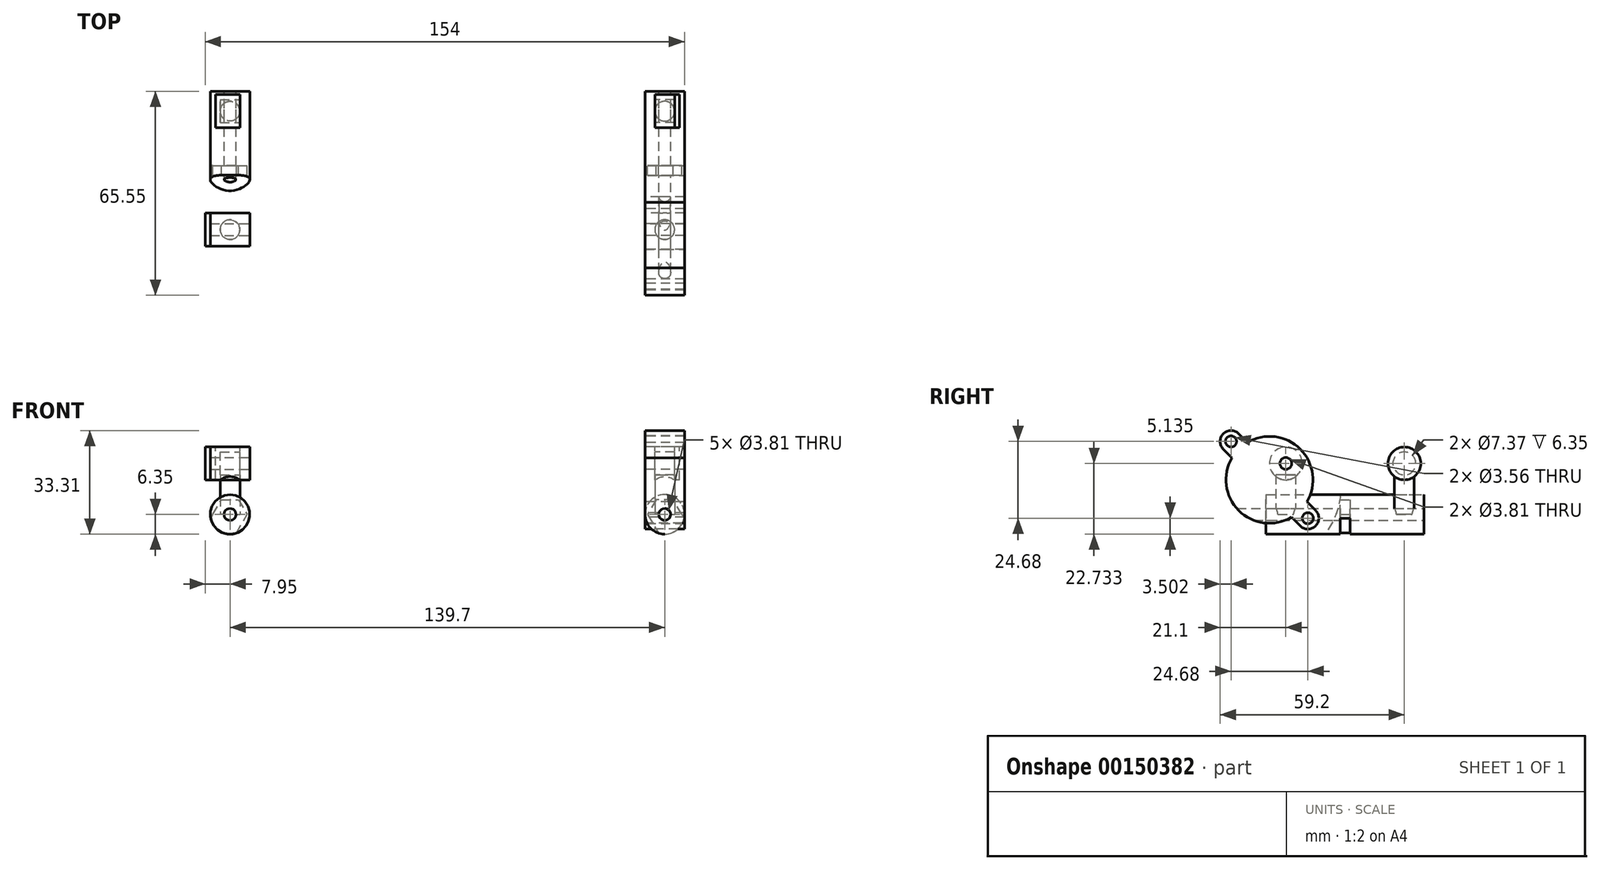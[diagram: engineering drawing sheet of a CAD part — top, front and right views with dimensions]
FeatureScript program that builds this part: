
annotation { "Feature Type Name" : "Feature", "Feature Type Description" : "" }
export const myFeature = defineFeature(function(context is Context, id is Id, definition is map)
    precondition{}
    {
        {
            var Q0;
            Q0=qCreatedBy(makeId("Front.planeOp"),FACE);
            var sketch = newSketch(context, id + "F0", { "sketchPlane" : qUnion([Q0])});
            skCircle(sketch, "E0", {"center": v(-69.85, 0) * mm, "radius": 1.9 * mm});
            skCircle(sketch, "E1", {"center": v(69.85, 0) * mm, "radius": 1.9 * mm});
            skLineSegment(sketch, "E2", {"start": v(-69.85, 0) * mm, "end": v(0, 0) * mm, "construction": true});
            skLineSegment(sketch, "E3", {"start": v(69.85, 0) * mm, "end": v(0, 0) * mm, "construction": true});
            skArc(sketch, "E4", {"start": v(-69.85, 6.35) * mm, "mid": v(-74.34, -4.5) * mm, "end": v(-63.5, 0) * mm});
            skArc(sketch, "E5", {"start": v(63.5, 0) * mm, "mid": v(74.34, -4.5) * mm, "end": v(69.85, 6.35) * mm});
            skLineSegment(sketch, "E6", {"start": v(69.85, 6.35) * mm, "end": v(69.85, 0) * mm, "construction": true});
            skLineSegment(sketch, "E7", {"start": v(-69.85, 6.35) * mm, "end": v(-69.85, 0) * mm, "construction": true});
            skArc(sketch, "E8", {"start": v(-63.5, 0) * mm, "mid": v(-65.36, 4.5) * mm, "end": v(-69.85, 6.35) * mm});
            skArc(sketch, "E9", {"start": v(69.85, 6.35) * mm, "mid": v(65.36, 4.5) * mm, "end": v(63.5, 0) * mm});
            skSolve(sketch);
        }
        {
            var Q0;
            Q0 = qSketchRegion(id + "F0", true);
            extrude(context, id + "F1", {"entities" : qUnion([Q0]), "endBound" : BoundingType.SYMMETRIC, "depth" : 12.7 * mm});
        }
        {
            var Q0;
            Q0=makeQuery(id+"F1.opExtrude","CAP_FACE",FACE,{"disambiguationData":[OSD([sQuery(id+"F0.wireOp",EDGE,"E0"),sQuery(id+"F0.wireOp",EDGE,"E1"),sQuery(id+"F0.wireOp",EDGE,"E4"),sQuery(id+"F0.wireOp",EDGE,"E5"),sQuery(id+"F0.wireOp",EDGE,"xyxUVOh0-Lu6m-2nq8-UmFe-XEndblqHEdPT"),sQuery(id+"F0.wireOp",EDGE,"R0XNFQHJ-87U4-ma3Q-qhns-AWXhGPeFOJpI"),sQuery(id+"F0.wireOp",EDGE,"e34iIN8D-vhv8-jKHx-9azW-8f77yfFPg5bW"),sQuery(id+"F0.wireOp",EDGE,"8HNf8llB-7DT9-wTKg-WSqf-SX1znclEPI6e"),sQuery(id+"F0.wireOp",EDGE,"dpBhEA3d-197v-VctA-TAhr-BlY7lmP6uD7G"),sQuery(id+"F0.wireOp",EDGE,"sEkqqTot-DNnZ-R70t-ELHf-v8sBDht2CAfZ")])],"isStart":false});
            var sketch = newSketch(context, id + "F2", { "sketchPlane" : qUnion([Q0])});
            skCircle(sketch, "E10.0", {"center": v(-69.85, 0) * mm, "radius": 1.9 * mm});
            skLineSegment(sketch, "E10.1", {"start": v(-64.48, 3.39) * mm, "end": v(-64.48, 3.39) * mm});
            skLineSegment(sketch, "E11.MirrorCS", {"start": v(64.48, 3.39) * mm, "end": v(64.48, 3.39) * mm});
            skCircle(sketch, "E12.MirrorC", {"center": v(69.85, 0) * mm, "radius": 1.9 * mm});
            skCircle(sketch, "E13.0", {"center": v(69.85, 0) * mm, "radius": 6.35 * mm});
            skCircle(sketch, "E13.1", {"center": v(-69.85, 0) * mm, "radius": 6.35 * mm});
            skSolve(sketch);
        }
        {
            var Q0;
            Q0 = qSketchRegion(id + "F2", true);
            extrude(context, id + "F3", {"entities" : qUnion([Q0]), "operationType" : NewBodyOperationType.ADD, "depth" : 19.05 * mm});
        }
        {
            var Q0;
            Q0=makeQuery(id+"F1.opExtrude","SWEPT_BODY",BODY,{"disambiguationData":[OSD([sQuery(id+"F0.wireOp",EDGE,"E0"),sQuery(id+"F0.wireOp",EDGE,"E1"),sQuery(id+"F0.wireOp",EDGE,"E4"),sQuery(id+"F0.wireOp",EDGE,"E5"),sQuery(id+"F0.wireOp",EDGE,"xyxUVOh0-Lu6m-2nq8-UmFe-XEndblqHEdPT"),sQuery(id+"F0.wireOp",EDGE,"R0XNFQHJ-87U4-ma3Q-qhns-AWXhGPeFOJpI"),sQuery(id+"F0.wireOp",EDGE,"e34iIN8D-vhv8-jKHx-9azW-8f77yfFPg5bW"),sQuery(id+"F0.wireOp",EDGE,"8HNf8llB-7DT9-wTKg-WSqf-SX1znclEPI6e"),sQuery(id+"F0.wireOp",EDGE,"dpBhEA3d-197v-VctA-TAhr-BlY7lmP6uD7G"),sQuery(id+"F0.wireOp",EDGE,"sEkqqTot-DNnZ-R70t-ELHf-v8sBDht2CAfZ")])]});
            var Q1;
            Q1=qCreatedBy(makeId("Front.planeOp"),FACE);
            mirror(context, id + "F4", {"operationType" : NewBodyOperationType.ADD, "entities" : qUnion([Q0]), "mirrorPlane" : qUnion([Q1])});
        }
        {
            var Q0;
            Q0=qCreatedBy(makeId("Front.planeOp"),FACE);
            var sketch = newSketch(context, id + "F5", { "sketchPlane" : qUnion([Q0])});
            skCircle(sketch, "E14.cCircle", {"center": v(-69.85, 0) * mm, "radius": 4.76 * mm, "construction": true});
            skLineSegment(sketch, "E14.0", {"start": v(-72.6, 4.76) * mm, "end": v(-67.1, 4.76) * mm});
            skLineSegment(sketch, "E14.1", {"start": v(-67.1, 4.76) * mm, "end": v(-64.35, 0) * mm});
            skLineSegment(sketch, "E14.2", {"start": v(-64.35, 0) * mm, "end": v(-67.1, -4.76) * mm});
            skLineSegment(sketch, "E14.5", {"start": v(-75.35, 0) * mm, "end": v(-72.6, 4.76) * mm});
            skPoint(sketch, "E14.0.midPoint", {"position": v(-69.85, 4.76) * mm});
            skLineSegment(sketch, "E15.MirrorCS", {"start": v(64.35, 0) * mm, "end": v(67.1, -4.76) * mm});
            skLineSegment(sketch, "E16.MirrorCS", {"start": v(75.35, 0) * mm, "end": v(72.6, 4.76) * mm});
            skLineSegment(sketch, "E17.MirrorCS", {"start": v(67.1, 4.76) * mm, "end": v(64.35, 0) * mm});
            skLineSegment(sketch, "E18.MirrorCS", {"start": v(72.6, 4.76) * mm, "end": v(67.1, 4.76) * mm});
            skCircle(sketch, "E19.MirrorC", {"center": v(69.85, 0) * mm, "radius": 4.76 * mm, "construction": true});
            skLineSegment(sketch, "E20", {"start": v(-75.35, 0) * mm, "end": v(-79.15, -6.2) * mm});
            skLineSegment(sketch, "E21", {"start": v(-79.15, -6.2) * mm, "end": v(-70.74, -11.07) * mm});
            skLineSegment(sketch, "E22", {"start": v(-70.74, -11.07) * mm, "end": v(-64.35, 0) * mm});
            skPoint(sketch, "E23.orphan", {"position": v(-72.6, -4.76) * mm});
            skLineSegment(sketch, "E24.MirrorCS", {"start": v(70.74, -11.07) * mm, "end": v(64.35, 0) * mm});
            skLineSegment(sketch, "E25.MirrorCS", {"start": v(75.35, 0) * mm, "end": v(79.15, -6.2) * mm});
            skLineSegment(sketch, "E26.MirrorCS", {"start": v(79.15, -6.2) * mm, "end": v(70.74, -11.07) * mm});
            skPoint(sketch, "E27.orphan", {"position": v(72.6, -4.76) * mm});
            skSolve(sketch);
        }
        {
            var Q0;
            Q0 = qSketchRegion(id + "F5", true);
            extrude(context, id + "F6", {"entities" : qUnion([Q0]), "operationType" : NewBodyOperationType.REMOVE, "endBound" : BoundingType.SYMMETRIC, "depth" : 3.17 * mm});
        }
        {
            var Q0;
            Q0=qCreatedBy(makeId("Top.planeOp"),FACE);
            var sketch = newSketch(context, id + "F7", { "sketchPlane" : qUnion([Q0])});
            skCircle(sketch, "E28", {"center": v(-69.85, 19.05) * mm, "radius": 3.18 * mm});
            skCircle(sketch, "E29.MirrorC", {"center": v(69.85, 19.05) * mm, "radius": 3.18 * mm});
            skCircle(sketch, "E30", {"center": v(-69.85, -19.05) * mm, "radius": 3.18 * mm});
            skLineSegment(sketch, "E31", {"start": v(-69.85, 19.05) * mm, "end": v(-69.85, -19.05) * mm, "construction": true});
            skCircle(sketch, "E32.MirrorC", {"center": v(69.85, -19.05) * mm, "radius": 3.18 * mm});
            skSolve(sketch);
        }
        {
            var Q0;
            Q0 = qSketchRegion(id + "F7", true);
            extrude(context, id + "F8", {"entities" : qUnion([Q0]), "depth" : 12.7 * mm});
        }
        {
            var Q0;
            Q0=makeQuery(id+"F4.opPattern","COPY",FACE,{"derivedFrom":makeQuery(id+"F3.opExtrude","CAP_FACE",FACE,{"disambiguationData":[OSD([sQuery(id+"F2.wireOp",EDGE,"E10.0"),sQuery(id+"F2.wireOp",EDGE,"E13.1")])],"isStart":false}),"instanceName":"1"});
            var sketch = newSketch(context, id + "F9", { "sketchPlane" : qUnion([Q0])});
            skCircle(sketch, "E33.0", {"center": v(69.85, 0) * mm, "radius": 1.9 * mm});
            skCircle(sketch, "E34.0", {"center": v(-69.85, 0) * mm, "radius": 1.9 * mm});
            skSolve(sketch);
        }
        {
            var Q0;
            Q0 = qSketchRegion(id + "F9", true);
            extrude(context, id + "F10", {"entities" : qUnion([Q0]), "operationType" : NewBodyOperationType.REMOVE, "oppositeDirection" : true, "depth" : 42.23 * mm});
        }
        {
            var Q0;
            Q0=qCreatedBy(makeId("Right.planeOp"),FACE);
            cPlane(context, id + "F11", {"entities" : qUnion([Q0]), "cplaneType" : CPlaneType.OFFSET, "offset" : 69.85 * mm, "width" : 152.4 * mm, "height" : 152.4 * mm});
        }
        {
            var Q0;
            Q0=qCreatedBy(id+"F11.planeOp",FACE);
            var sketch = newSketch(context, id + "F12", { "sketchPlane" : qUnion([Q0])});
            skCircle(sketch, "E35", {"center": v(19.05, 16.38) * mm, "radius": 5.28 * mm});
            skCircle(sketch, "E36", {"center": v(19.05, 16.38) * mm, "radius": 3.68 * mm});
            skSolve(sketch);
        }
        {
            var Q0;
            Q0 = qSketchRegion(id + "F12", true);
            extrude(context, id + "F13", {"entities" : qUnion([Q0]), "endBound" : BoundingType.SYMMETRIC, "depth" : 6.35 * mm});
        }
        {
            var Q0;
            Q0=makeQuery(id+"F13.opExtrude","SWEPT_BODY",BODY,{"disambiguationData":[OSD([sQuery(id+"F12.wireOp",EDGE,"E35"),sQuery(id+"F12.wireOp",EDGE,"E36")])]});
            var Q1;
            Q1=qCreatedBy(makeId("Right.planeOp"),FACE);
            mirror(context, id + "F14", {"operationType" : NewBodyOperationType.ADD, "entities" : qUnion([Q0]), "mirrorPlane" : qUnion([Q1])});
        }
        {
            var Q0;
            Q0=makeQuery(id+"F13.opExtrude","CAP_FACE",FACE,{"disambiguationData":[OSD([sQuery(id+"F12.wireOp",EDGE,"E35"),sQuery(id+"F12.wireOp",EDGE,"E36")])],"isStart":false});
            var sketch = newSketch(context, id + "F15", { "sketchPlane" : qUnion([Q0])});
            skCircle(sketch, "E37.0", {"center": v(19.05, 16.38) * mm, "radius": 5.28 * mm});
            skSolve(sketch);
        }
        {
            var Q0;
            Q0 = qSketchRegion(id + "F15", true);
            extrude(context, id + "F16", {"entities" : qUnion([Q0]), "depth" : 1.52 * mm});
        }
        {
            var Q0;
            Q0=makeQuery(id+"F14.opPattern","COPY",FACE,{"derivedFrom":makeQuery(id+"F13.opExtrude","CAP_FACE",FACE,{"disambiguationData":[OSD([sQuery(id+"F12.wireOp",EDGE,"E35"),sQuery(id+"F12.wireOp",EDGE,"E36")])],"isStart":false}),"instanceName":"1"});
            var sketch = newSketch(context, id + "F17", { "sketchPlane" : qUnion([Q0])});
            skCircle(sketch, "E38.0", {"center": v(-19.05, 16.38) * mm, "radius": 5.28 * mm});
            skSolve(sketch);
        }
        {
            var Q0;
            Q0 = qSketchRegion(id + "F17", true);
            extrude(context, id + "F18", {"entities" : qUnion([Q0]), "operationType" : NewBodyOperationType.ADD, "depth" : 1.52 * mm});
        }
        {
            var Q0;
            Q0=qCreatedBy(id+"F11.planeOp",FACE);
            var sketch = newSketch(context, id + "F19", { "sketchPlane" : qUnion([Q0])});
            skCircle(sketch, "E39", {"center": v(-19.05, 16.38) * mm, "radius": 1.9 * mm});
            skLineSegment(sketch, "E40", {"start": v(13.77, 16.38) * mm, "end": v(-19.05, 16.38) * mm, "construction": true});
            skCircle(sketch, "E41.0", {"center": v(19.05, 16.38) * mm, "radius": 5.28 * mm, "construction": true});
            skLineSegment(sketch, "E42", {"start": v(19.05, 16.38) * mm, "end": v(13.77, 16.38) * mm, "construction": true});
            skArc(sketch, "E43", {"start": v(-36.35, 18.21) * mm, "mid": v(-34.19, 1.25) * mm, "end": v(-17.22, -0.91) * mm});
            skArc(sketch, "E44", {"start": v(-34.17, 25.94) * mm, "mid": v(-39.12, 25.94) * mm, "end": v(-39.12, 20.99) * mm});
            skArc(sketch, "E45", {"start": v(-14.44, -3.69) * mm, "mid": v(-9.5, -3.69) * mm, "end": v(-9.5, 1.26) * mm});
            skLineSegment(sketch, "E46", {"start": v(-36.65, 23.46) * mm, "end": v(-24.3, 11.13) * mm, "construction": true});
            skLineSegment(sketch, "E47", {"start": v(-24.3, 11.13) * mm, "end": v(-11.97, -1.21) * mm, "construction": true});
            skLineSegment(sketch, "E48", {"start": v(-19.05, 16.38) * mm, "end": v(-14.43, 21) * mm, "construction": true});
            skLineSegment(sketch, "E49", {"start": v(-36.65, 23.46) * mm, "end": v(-19.05, 16.38) * mm, "construction": true});
            skLineSegment(sketch, "E50", {"start": v(-19.05, 16.38) * mm, "end": v(-11.97, -1.21) * mm, "construction": true});
            skLineSegment(sketch, "E51", {"start": v(-39.12, 20.99) * mm, "end": v(-36.35, 18.21) * mm});
            skLineSegment(sketch, "E52", {"start": v(-34.17, 25.94) * mm, "end": v(-31.4, 23.16) * mm});
            skLineSegment(sketch, "E53", {"start": v(-39.12, 20.99) * mm, "end": v(-36.65, 23.46) * mm, "construction": true});
            skLineSegment(sketch, "E54", {"start": v(-34.17, 25.94) * mm, "end": v(-36.65, 23.46) * mm, "construction": true});
            skLineSegment(sketch, "E55", {"start": v(-14.44, -3.69) * mm, "end": v(-17.22, -0.91) * mm});
            skLineSegment(sketch, "E56", {"start": v(-9.5, 1.26) * mm, "end": v(-12.27, 4.04) * mm});
            skLineSegment(sketch, "E57", {"start": v(-14.44, -3.69) * mm, "end": v(-11.97, -1.21) * mm, "construction": true});
            skLineSegment(sketch, "E58", {"start": v(-11.97, -1.21) * mm, "end": v(-9.5, 1.26) * mm, "construction": true});
            skArc(sketch, "E59.trimOffspring", {"start": v(-12.27, 4.04) * mm, "mid": v(-14.43, 21) * mm, "end": v(-31.4, 23.16) * mm});
            skCircle(sketch, "E60", {"center": v(-36.65, 23.46) * mm, "radius": 1.78 * mm});
            skCircle(sketch, "E61.MirrorC", {"center": v(-11.97, -1.21) * mm, "radius": 1.78 * mm});
            skSolve(sketch);
        }
        {
            var Q0;
            Q0 = qSketchRegion(id + "F19", true);
            extrude(context, id + "F20", {"entities" : qUnion([Q0]), "endBound" : BoundingType.SYMMETRIC, "depth" : 12.7 * mm});
        }
        {
            var Q0;
            Q0=makeQuery(id+"F20.opExtrude","SWEPT_BODY",BODY,{"disambiguationData":[OSD([sQuery(id+"F19.wireOp",EDGE,"E39"),sQuery(id+"F19.wireOp",EDGE,"E43"),sQuery(id+"F19.wireOp",EDGE,"E44"),sQuery(id+"F19.wireOp",EDGE,"E45"),sQuery(id+"F19.wireOp",EDGE,"E51"),sQuery(id+"F19.wireOp",EDGE,"E52"),sQuery(id+"F19.wireOp",EDGE,"E55"),sQuery(id+"F19.wireOp",EDGE,"E56"),sQuery(id+"F19.wireOp",EDGE,"E59.trimOffspring")])]});
            var Q1;
            Q1=qCreatedBy(makeId("Right.planeOp"),FACE);
            mirror(context, id + "F21", {"entities" : qUnion([Q0]), "mirrorPlane" : qUnion([Q1])});
        }
        {
            var Q0;
            Q0=makeQuery(id+"F21.opPattern","COPY",FACE,{"derivedFrom":makeQuery(id+"F20.opExtrude","CAP_FACE",FACE,{"disambiguationData":[OSD([sQuery(id+"F19.wireOp",EDGE,"E39"),sQuery(id+"F19.wireOp",EDGE,"E43"),sQuery(id+"F19.wireOp",EDGE,"E44"),sQuery(id+"F19.wireOp",EDGE,"E45"),sQuery(id+"F19.wireOp",EDGE,"E51"),sQuery(id+"F19.wireOp",EDGE,"E52"),sQuery(id+"F19.wireOp",EDGE,"E55"),sQuery(id+"F19.wireOp",EDGE,"E56"),sQuery(id+"F19.wireOp",EDGE,"E59.trimOffspring")])],"isStart":false}),"instanceName":"1"});
            var sketch = newSketch(context, id + "F22", { "sketchPlane" : qUnion([Q0])});
            skCircle(sketch, "E62", {"center": v(19.05, 16.38) * mm, "radius": 5.28 * mm});
            skCircle(sketch, "E63", {"center": v(25.47, 8.62) * mm, "radius": 24.12 * mm});
            skSolve(sketch);
        }
        {
            var Q0;
            Q0 = qSketchRegion(id + "F22", true);
            extrude(context, id + "F23", {"entities" : qUnion([Q0]), "operationType" : NewBodyOperationType.REMOVE, "oppositeDirection" : true, "depth" : 25.4 * mm});
        }
        {
            var Q0;
            Q0=makeQuery(id+"F21.opPattern","COPY",FACE,{"derivedFrom":makeQuery(id+"F20.opExtrude","CAP_FACE",FACE,{"disambiguationData":[OSD([sQuery(id+"F19.wireOp",EDGE,"E39"),sQuery(id+"F19.wireOp",EDGE,"E43"),sQuery(id+"F19.wireOp",EDGE,"E44"),sQuery(id+"F19.wireOp",EDGE,"E45"),sQuery(id+"F19.wireOp",EDGE,"E51"),sQuery(id+"F19.wireOp",EDGE,"E52"),sQuery(id+"F19.wireOp",EDGE,"E55"),sQuery(id+"F19.wireOp",EDGE,"E56"),sQuery(id+"F19.wireOp",EDGE,"E59.trimOffspring")])],"isStart":false}),"instanceName":"1"});
            var sketch = newSketch(context, id + "F24", { "sketchPlane" : qUnion([Q0])});
            skCircle(sketch, "E64.0", {"center": v(19.05, 16.38) * mm, "radius": 5.28 * mm});
            skSolve(sketch);
        }
        {
            var Q0;
            Q0 = qSketchRegion(id + "F24", true);
            extrude(context, id + "F25", {"entities" : qUnion([Q0]), "depth" : 1.6 * mm});
        }
        {
            var Q0;
            Q0=makeQuery(id+"F4.opPattern","COPY",FACE,{"derivedFrom":makeQuery(id+"F3.opExtrude","CAP_FACE",FACE,{"disambiguationData":[OSD([sQuery(id+"F2.wireOp",EDGE,"E12.MirrorC"),sQuery(id+"F2.wireOp",EDGE,"E13.0")])],"isStart":false}),"instanceName":"1"});
            var sketch = newSketch(context, id + "F26", { "sketchPlane" : qUnion([Q0])});
            skCircle(sketch, "E65.0", {"center": v(-69.85, 0) * mm, "radius": 1.9 * mm});
            skCircle(sketch, "E66.0", {"center": v(69.85, 0) * mm, "radius": 1.9 * mm});
            skSolve(sketch);
        }
        {
            var Q0;
            Q0 = qSketchRegion(id + "F26", true);
            extrude(context, id + "F27", {"entities" : qUnion([Q0]), "operationType" : NewBodyOperationType.REMOVE, "oppositeDirection" : true, "depth" : 77.1 * mm});
        }
    });
